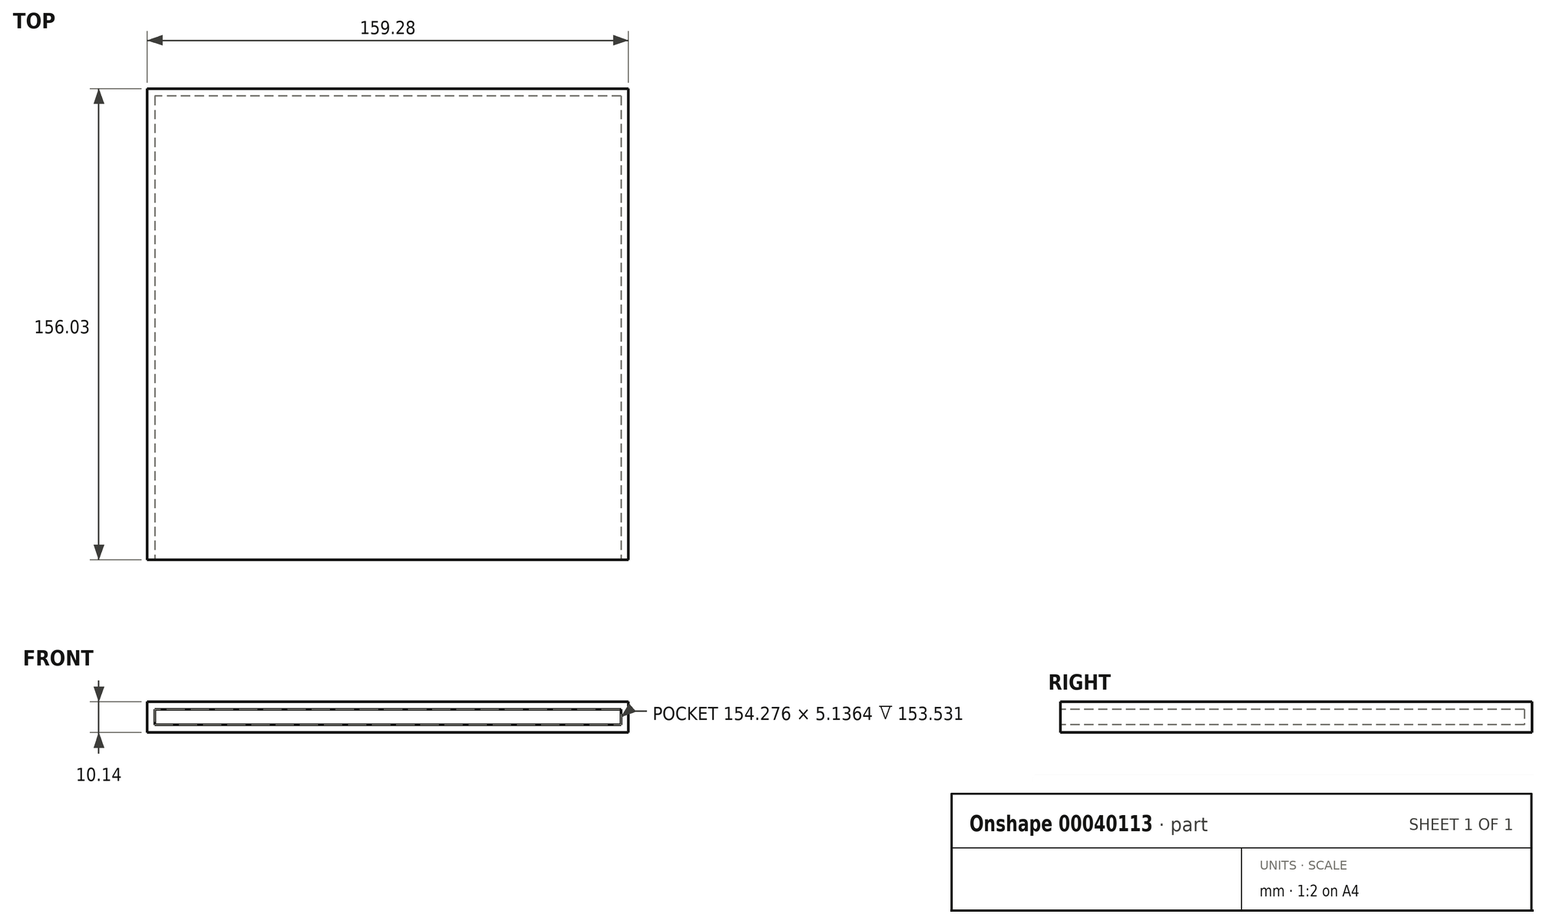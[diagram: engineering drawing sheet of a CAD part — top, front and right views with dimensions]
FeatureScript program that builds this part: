
annotation { "Feature Type Name" : "Feature", "Feature Type Description" : "" }
export const myFeature = defineFeature(function(context is Context, id is Id, definition is map)
    precondition{}
    {
        {
            var Q0;
            Q0=qCreatedBy(makeId("Top.planeOp"),FACE);
            var sketch = newSketch(context, id + "F0", { "sketchPlane" : qUnion([Q0])});
            skCircle(sketch, "E0", {"center": v(0, 0) * mm, "radius": 74.9 * mm});
            skSolve(sketch);
        }
        {
            var Q0;
            Q0=makeQuery(id+"F0.imprint","IMPRINT",FACE,{"disambiguationData":[TD([[makeQuery(id+"F0.imprint","IMPRINT",EDGE,{"derivedFrom":sQuery(id+"F0.wireOp",EDGE,"E0")}),1.0]])]});
            extrude(context, id + "F1", {"entities" : qUnion([Q0]), "depth" : 1.78 * mm});
        }
        {
            var Q0;
            Q0=qCreatedBy(makeId("Top.planeOp"),FACE);
            var sketch = newSketch(context, id + "F2", { "sketchPlane" : qUnion([Q0])});
            skLineSegment(sketch, "E1.bottom", {"start": v(77.42, 76.65) * mm, "end": v(-76.86, 76.65) * mm});
            skLineSegment(sketch, "E1.top", {"start": v(77.42, -76.88) * mm, "end": v(-76.86, -76.88) * mm});
            skLineSegment(sketch, "E1.left", {"start": v(77.42, 76.65) * mm, "end": v(77.42, -76.88) * mm});
            skLineSegment(sketch, "E1.right", {"start": v(-76.86, 76.65) * mm, "end": v(-76.86, -76.88) * mm});
            skSolve(sketch);
        }
        {
            var Q0;
            Q0=makeQuery(id+"F2.imprint","IMPRINT",FACE,{"disambiguationData":[TD([[makeQuery(id+"F2.imprint","IMPRINT",EDGE,{"derivedFrom":sQuery(id+"F2.wireOp",EDGE,"E1.bottom")}),1.0]])]});
            extrude(context, id + "F3", {"entities" : qUnion([Q0]), "operationType" : NewBodyOperationType.ADD, "depth" : 5.14 * mm});
        }
        {
            var Q0;
            Q0=makeQuery(id+"F3.opExtrude","SWEPT_FACE",FACE,{"disambiguationData":[OSD([sQuery(id+"F2.wireOp",EDGE,"E1.top")])]});
            shell(context, id + "F4", {"entities" : qUnion([Q0]), "thickness" : 2.5 * mm, "oppositeDirection" : true});
        }
    });
